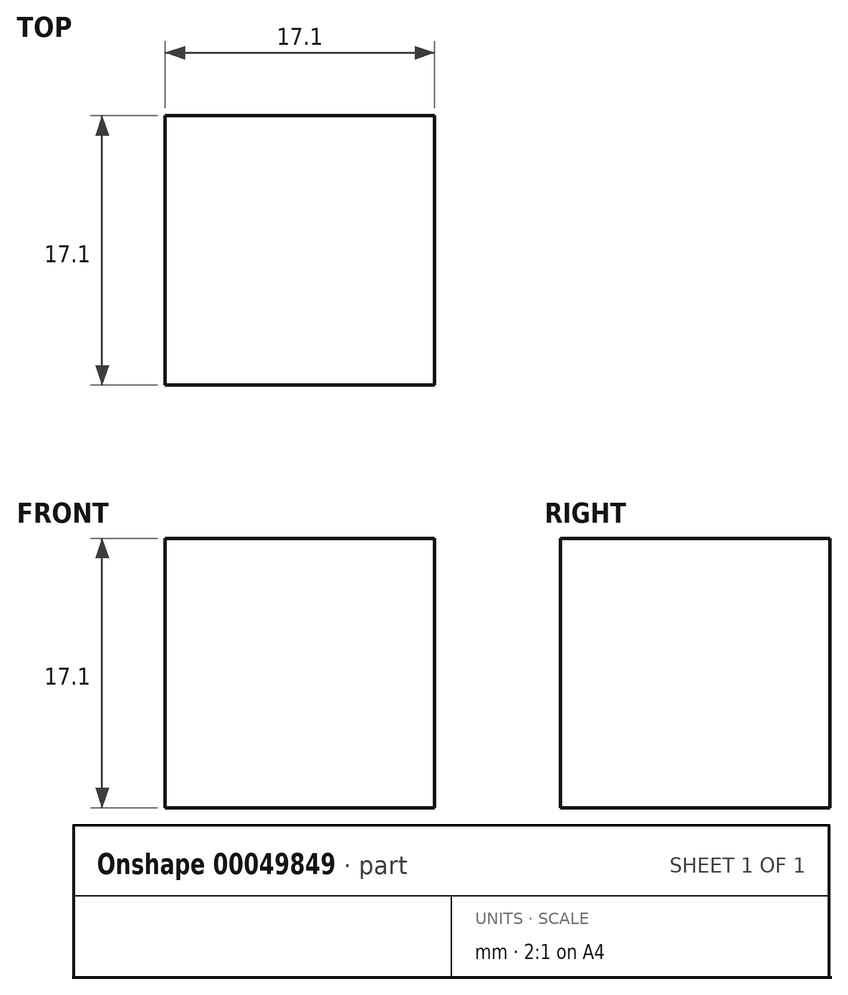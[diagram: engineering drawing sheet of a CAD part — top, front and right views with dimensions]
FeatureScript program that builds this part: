
annotation { "Feature Type Name" : "Feature", "Feature Type Description" : "" }
export const myFeature = defineFeature(function(context is Context, id is Id, definition is map)
    precondition{}
    {
        {
            var Q0;
            Q0=qCreatedBy(makeId("Top.planeOp"),FACE);
            var sketch = newSketch(context, id + "F0", { "sketchPlane" : qUnion([Q0])});
            skLineSegment(sketch, "E0.rect.bottom", {"start": v(8.55, 8.55) * mm, "end": v(-8.55, 8.55) * mm});
            skLineSegment(sketch, "E0.rect.top", {"start": v(8.55, -8.55) * mm, "end": v(-8.55, -8.55) * mm});
            skLineSegment(sketch, "E0.rect.left", {"start": v(8.55, 8.55) * mm, "end": v(8.55, -8.55) * mm});
            skLineSegment(sketch, "E0.rect.right", {"start": v(-8.55, 8.55) * mm, "end": v(-8.55, -8.55) * mm});
            skPoint(sketch, "E0.rect.middle", {"position": v(0, 0) * mm});
            skSolve(sketch);
        }
        {
            var Q0;
            Q0=makeQuery(id+"F0.imprint","IMPRINT",FACE,{"disambiguationData":[TD([[makeQuery(id+"F0.imprint","IMPRINT",EDGE,{"derivedFrom":sQuery(id+"F0.wireOp",EDGE,"E0.rect.bottom")}),1.0]])]});
            extrude(context, id + "F1", {"entities" : qUnion([Q0]), "depth" : 17.1 * mm});
        }
    });
